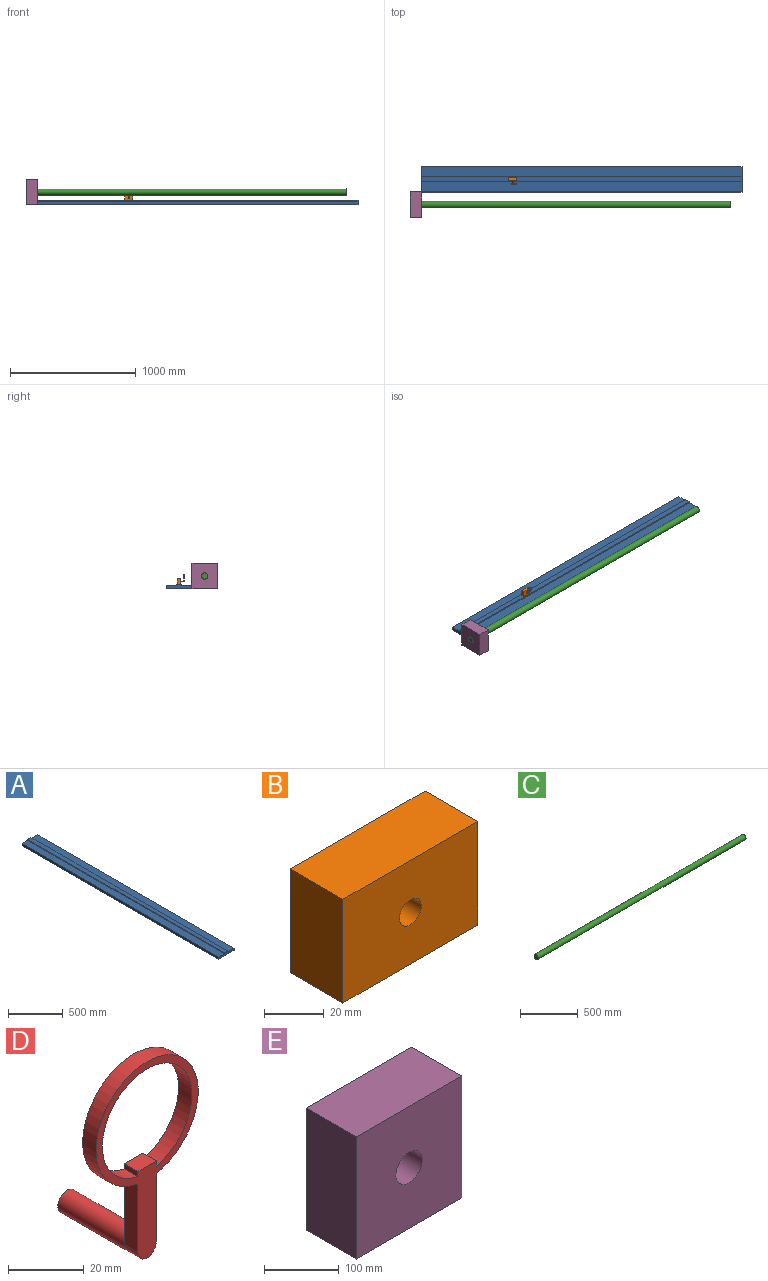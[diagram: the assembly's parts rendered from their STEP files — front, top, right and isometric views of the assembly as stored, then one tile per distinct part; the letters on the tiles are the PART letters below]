
ASSEMBLY  parts=5 mates=4
PART A: 10 faces, bbox 200x2540x35 mm
  f0: plane 2540x74.67mm, normal (0,0,1), area 189653mm2, adj f2,f5,f6,f8
  f1: plane 2540x83.8mm, normal (0,0,1), area 212839.3mm2, adj f4,f5,f6,f7
  f2: plane 2540x25mm, normal (-1,0,0), area 63500mm2, adj f0,f3,f5,f6
  f3: plane 2540x200mm, normal (0,0,-1), area 508000mm2, adj f2,f4,f5,f6
  f4: plane 2540x25mm, normal (1,0,0), area 63500mm2, adj f1,f3,f5,f6
  f5: plane 200x35.02mm, normal (0,-1,0), area 5416.2mm2, adj f0,f1,f2,f3,f4,f7,f8,f9
  f6: plane 200x35.02mm, normal (0,1,0), area 5416.2mm2, adj f0,f1,f2,f3,f4,f7,f8,f9
  f7: plane 2540x10.02mm, normal (1,0,0), area 25448.3mm2, adj f1,f5,f6,f9
  f8: plane 2540x10.02mm, normal (-1,0,0), area 25448.3mm2, adj f0,f5,f6,f9
  f9: plane 2540x41.54mm, normal (0,0,1), area 105507.7mm2, adj f5,f6,f7,f8
PART B: 7 faces, bbox 64x25x42.6 mm
  f0: plane 42.55x25mm, normal (-1,0,0), area 1063.8mm2, adj f1,f3,f5,f6
  f1: plane 63.96x25mm, normal (0,0,-1), area 1599mm2, adj f0,f2,f5,f6
  f2: plane 42.55x25mm, normal (1,0,0), area 1063.8mm2, adj f1,f3,f5,f6
  f3: plane 63.96x25mm, normal (0,0,1), area 1599mm2, adj f0,f2,f5,f6
  f4: cylinder r=5.17mm len=25mm, axis (0,1,0), area 812.2mm2, adj f5,f6
  f5: plane 63.96x42.55mm, normal (0,-1,0), area 2637.7mm2, adj f0,f1,f2,f3,f4
  f6: plane 63.96x42.55mm, normal (0,1,0), area 2637.7mm2, adj f0,f1,f2,f3,f4
PART C: 3 faces, bbox 2540x51.6x51.6 mm
  f0: cylinder r=25.8mm len=2540mm, axis (-1,0,0), area 411768mm2, adj f1,f2
  f1: plane 51.6x51.6mm, normal (1,0,0), area 2091.4mm2, adj f0
  f2: plane 51.6x51.6mm, normal (-1,0,0), area 2091.4mm2, adj f0
PART D: 11 faces, bbox 38.2x30x63.6 mm
  f0: plane 5x1.66mm, normal (1,0,0), area 8.3mm2, adj f4,f6,f8,f10
  f1: plane 5x1.66mm, normal (-1,0,0), area 8.3mm2, adj f4,f6,f8,f10
  f2: cylinder r=3.42mm len=30mm, axis (0,1,0), area 590.7mm2, adj f3,f4,f5,f7,f8
  f3: plane 6.84x6.84mm, normal (0,1,0), area 36.7mm2, adj f2
  f4: plane 60.14x38.24mm, normal (0,1,0), area 410.5mm2, adj f0,f1,f2,f5,f6,f7,f9,f10
  f5: plane 22.21x5mm, normal (1,0,0), area 111mm2, adj f2,f4,f8,f9
  f6: plane 6.84x5mm, normal (0,0,1), area 34.2mm2, adj f0,f1,f4,f8
  f7: plane 22.21x5mm, normal (-1,0,0), area 111mm2, adj f2,f4,f8,f9
  f8: plane 63.56x38.24mm, normal (0,-1,0), area 447.2mm2, adj f0,f1,f2,f5,f6,f7,f9,f10
  f9: cylinder r=19.12mm len=38.24mm, axis (0,-1,0), area 566.3mm2, adj f4,f5,f7,f8
  f10: cylinder r=16.76mm len=33.53mm, axis (0,-1,0), area 492.2mm2, adj f0,f1,f4,f8
PART E: 7 faces, bbox 200x95x200 mm
  f0: plane 200x95mm, normal (-1,0,0), area 19000mm2, adj f1,f3,f5,f6
  f1: plane 200x95mm, normal (0,0,-1), area 19000mm2, adj f0,f2,f5,f6
  f2: plane 200x95mm, normal (1,0,0), area 19000mm2, adj f1,f3,f5,f6
  f3: plane 200x95mm, normal (0,0,1), area 19000mm2, adj f0,f2,f5,f6
  f4: cylinder r=25mm len=95mm, axis (0,1,0), area 14922.6mm2, adj f5,f6
  f5: plane 200x200mm, normal (0,-1,0), area 38036.5mm2, adj f0,f1,f2,f3,f4
  f6: plane 200x200mm, normal (0,1,0), area 38036.5mm2, adj f0,f1,f2,f3,f4
PLACE A rot(axis=(0,0,-1),90deg) t=(3519.25,202.78,-326.68)mm
PLACE B t=(1668.89,260.56,-304.79)mm
PLACE C t=(884.25,43.5,-239.81)mm
PLACE D rot(axis=(0,1,0),10deg) t=(1665.68,260.56,-298.91)mm
PLACE E rot(axis=(-0.58,-0.58,-0.58),120deg) t=(979.25,-21.16,-296.39)mm fixed
MATE fastened A.f5 <-> E.f6  axis (-1,0,0) through (979.25,143.5,-339.81)mm
MATE slider B.f2 <-> A.f6  axis (1,0,0) through (1732.85,248.06,-304.79)mm
MATE revolute E.f4 <-> C.f0  axis (-1,0,0) through (884.25,43.5,-239.81)mm
MATE revolute D.f2 <-> B.f4  axis (0,1,0) through (1700.87,235.56,-283.51)mm
